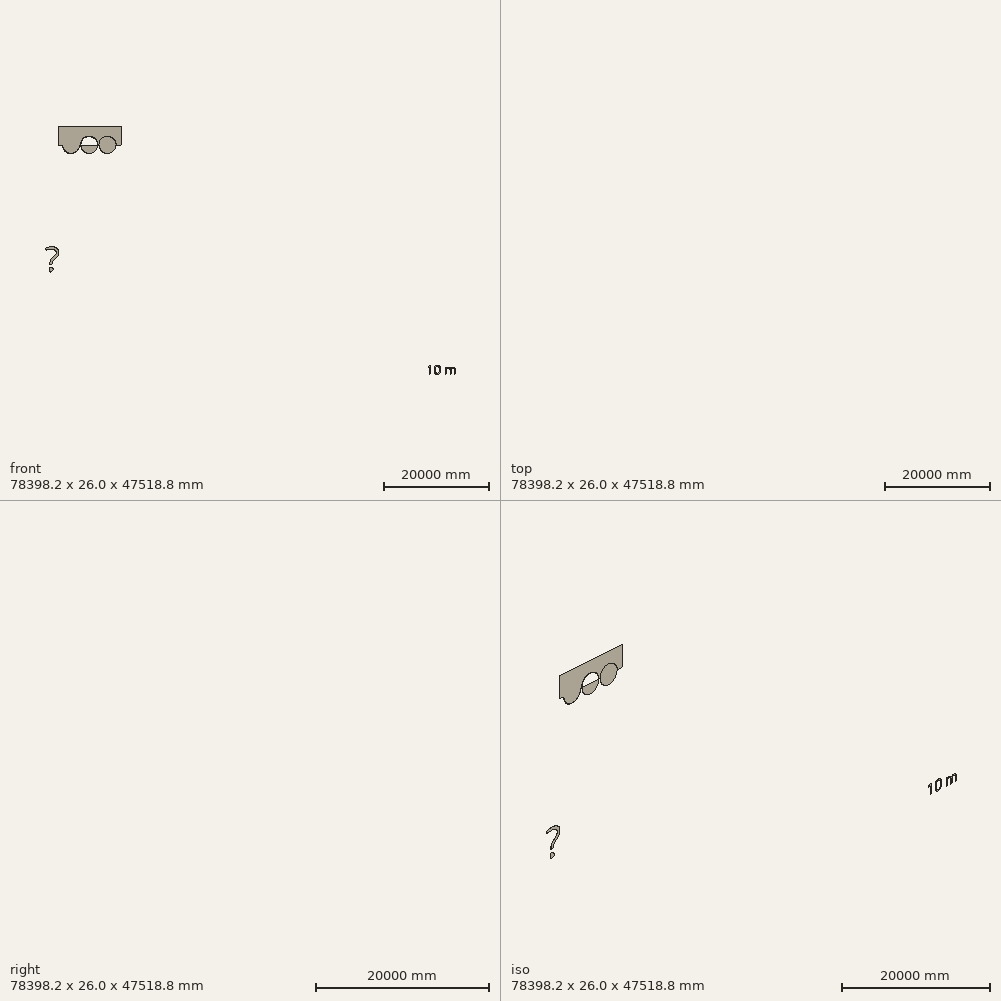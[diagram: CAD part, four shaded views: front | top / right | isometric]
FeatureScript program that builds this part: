
annotation { "Feature Type Name" : "Feature", "Feature Type Description" : "" }
export const myFeature = defineFeature(function(context is Context, id is Id, definition is map)
    precondition{}
    {
        {
            var Q0;
            Q0=qCreatedBy(makeId("Front.planeOp"),FACE);
            var sketch = newSketch(context, id + "F0", { "sketchPlane" : qUnion([Q0])});
            skLineSegment(sketch, "E0", {"start": v(18624.53, 0) * mm, "end": v(-26282.53, 0) * mm});
            skLineSegment(sketch, "E1", {"start": v(-54535.88, 46620.48) * mm, "end": v(-44660.11, 46620.48) * mm});
            skLineSegment(sketch, "E2", {"start": v(-34660.11, 36620.48) * mm, "end": v(-34660.11, 26407.32) * mm});
            skLineSegment(sketch, "E3", {"start": v(-34660.11, 26407.32) * mm, "end": v(-34660.11, 23210.3) * mm});
            skLineSegment(sketch, "E4", {"start": v(-34660.11, 23210.3) * mm, "end": v(-34660.11, 20000) * mm});
            skLineSegment(sketch, "E5", {"start": v(-14660.11, 0) * mm, "end": v(-1994.16, 0) * mm});
            skLineSegment(sketch, "E6", {"start": v(3005.84, 4000) * mm, "end": v(3005.84, 5000) * mm});
            skLineSegment(sketch, "E7", {"start": v(9005.84, 10000) * mm, "end": v(15278.8, 10000) * mm});
            skPoint(sketch, "E8.visualSharp", {"position": v(-34660.11, 46620.48) * mm});
            skArc(sketch, "E8.filletArc", {"start": v(-34660.11, 36620.48) * mm, "mid": v(-37589.04, 43691.54) * mm, "end": v(-44660.11, 46620.48) * mm});
            skPoint(sketch, "E9.visualSharp", {"position": v(-34660.11, 0) * mm});
            skArc(sketch, "E9.filletArc", {"start": v(-34660.11, 20000) * mm, "mid": v(-28802.25, 5857.86) * mm, "end": v(-14660.11, 0) * mm});
            skPoint(sketch, "E10.visualSharp", {"position": v(3005.84, 0) * mm});
            skArc(sketch, "E10.filletArc", {"start": v(-1994.16, 0) * mm, "mid": v(1541.37, 1464.47) * mm, "end": v(3005.84, 5000) * mm});
            skPoint(sketch, "E11.visualSharp", {"position": v(3005.84, 10000) * mm});
            skArc(sketch, "E11.filletArc", {"start": v(9005.84, 10000) * mm, "mid": v(4763.2, 8242.64) * mm, "end": v(3005.84, 4000) * mm});
            skCircle(sketch, "E12", {"center": v(-49592.93, 48230.24) * mm, "radius": 1609.76 * mm});
            skCircle(sketch, "E13", {"center": v(-46111.93, 48230.24) * mm, "radius": 1609.76 * mm});
            skLineSegment(sketch, "E14.bottom", {"start": v(-43471.17, 48230.24) * mm, "end": v(-55474.63, 48230.24) * mm});
            skLineSegment(sketch, "E14.top", {"start": v(-43471.17, 51831.28) * mm, "end": v(-55474.63, 51831.28) * mm});
            skLineSegment(sketch, "E14.left", {"start": v(-43471.17, 48230.24) * mm, "end": v(-43471.17, 51831.28) * mm});
            skLineSegment(sketch, "E14.right", {"start": v(-55474.63, 48230.24) * mm, "end": v(-55474.63, 51831.28) * mm});
            skCircle(sketch, "E15", {"center": v(-53073.94, 48230.24) * mm, "radius": 1609.76 * mm});
            skSolve(sketch);
        }
        {
            var Q0;
            Q0=sQuery(id+"F0.wireOp",EDGE,"E1");
            var Q1;
            Q1=sQuery(id+"F0.wireOp",EDGE,"E2");
            var Q2;
            Q2=sQuery(id+"F0.wireOp",EDGE,"E3");
            var Q3;
            Q3=sQuery(id+"F0.wireOp",EDGE,"E4");
            var Q4;
            Q4=sQuery(id+"F0.wireOp",EDGE,"E6");
            var Q5;
            Q5=sQuery(id+"F0.wireOp",EDGE,"E7");
            var Q6;
            Q6=sQuery(id+"F0.wireOp",EDGE,"E8.filletArc");
            var Q7;
            Q7=sQuery(id+"F0.wireOp",EDGE,"E10.filletArc");
            var Q8;
            Q8=sQuery(id+"F0.wireOp",EDGE,"E11.filletArc");
            var Q9;
            Q9=sQuery(id+"F0.wireOp",EDGE,"E9.filletArc");
            var Q10;
            Q10=sQuery(id+"F0.wireOp",EDGE,"E5");
            extrude(context, id + "F1", {"bodyType" : ToolBodyType.SURFACE, "surfaceEntities" : qUnion([Q0, Q1, Q2, Q3, Q4, Q5, Q6, Q7, Q8, Q9, Q10]), "endBound" : BoundingType.SYMMETRIC, "depth" : 1000 * mm});
        }
        {
            var Q0;
            Q0=makeQuery(id+"F0.imprint","IMPRINT",FACE,{"disambiguationData":[TD([[makeQuery(id+"F0.imprint","IMPRINT",EDGE,{"derivedFrom":sQuery(id+"F0.wireOp",EDGE,"E14.top")}),1.0]])]});
            var Q1;
            {var subQ0=sQuery(id+"F0.wireOp",EDGE,"E14.bottom");var subQ1=sQuery(id+"F0.wireOp",EDGE,"E13");var subQ2=makeQuery(id+"F0.imprint","INTERSECT",VERTEX,{"disambiguationData":[OD(0.0)],"derivedFrom":[subQ1,subQ0]});Q1=makeQuery(id+"F0.imprint","IMPRINT",FACE,{"disambiguationData":[TD([[makeQuery(id+"F0.imprint","IMPRINT",EDGE,{"disambiguationData":[TD([[subQ2,-1.0]])],"derivedFrom":subQ1}),1.0]])]});}
            var Q2;
            {var subQ0=sQuery(id+"F0.wireOp",EDGE,"E13");var subQ1=makeQuery(id+"F0.imprint","INTERSECT",VERTEX,{"derivedFrom":[sQuery(id+"F0.wireOp",EDGE,"E1"),subQ0]});Q2=makeQuery(id+"F0.imprint","IMPRINT",FACE,{"disambiguationData":[TD([[makeQuery(id+"F0.imprint","IMPRINT",EDGE,{"disambiguationData":[TD([[subQ1,1.0]])],"derivedFrom":subQ0}),1.0]])]});}
            var Q3;
            {var subQ0=sQuery(id+"F0.wireOp",EDGE,"E12");var subQ1=makeQuery(id+"F0.imprint","INTERSECT",VERTEX,{"derivedFrom":[sQuery(id+"F0.wireOp",EDGE,"E1"),subQ0]});Q3=makeQuery(id+"F0.imprint","IMPRINT",FACE,{"disambiguationData":[TD([[makeQuery(id+"F0.imprint","IMPRINT",EDGE,{"disambiguationData":[TD([[subQ1,1.0]])],"derivedFrom":subQ0}),1.0]])]});}
            var Q4;
            {var subQ0=sQuery(id+"F0.wireOp",EDGE,"E14.bottom");var subQ1=sQuery(id+"F0.wireOp",EDGE,"E12");var subQ2=makeQuery(id+"F0.imprint","INTERSECT",VERTEX,{"disambiguationData":[OD(0.0)],"derivedFrom":[subQ1,subQ0]});Q4=makeQuery(id+"F0.imprint","IMPRINT",FACE,{"disambiguationData":[TD([[makeQuery(id+"F0.imprint","IMPRINT",EDGE,{"disambiguationData":[TD([[subQ2,1.0]])],"derivedFrom":subQ1}),1.0]])]});}
            var Q5;
            {var subQ0=sQuery(id+"F0.wireOp",EDGE,"E15");var subQ1=sQuery(id+"F0.wireOp",EDGE,"E14.bottom");var subQ2=makeQuery(id+"F0.imprint","INTERSECT",VERTEX,{"disambiguationData":[OD(0.0)],"derivedFrom":[subQ1,subQ0]});Q5=makeQuery(id+"F0.imprint","IMPRINT",FACE,{"disambiguationData":[TD([[makeQuery(id+"F0.imprint","IMPRINT",EDGE,{"disambiguationData":[TD([[subQ2,1.0]])],"derivedFrom":subQ1}),1.0]])]});}
            var Q6;
            {var subQ0=sQuery(id+"F0.wireOp",EDGE,"E15");var subQ1=sQuery(id+"F0.wireOp",EDGE,"E14.bottom");var subQ2=makeQuery(id+"F0.imprint","INTERSECT",VERTEX,{"disambiguationData":[OD(0.0)],"derivedFrom":[subQ1,subQ0]});Q6=makeQuery(id+"F0.imprint","IMPRINT",FACE,{"disambiguationData":[TD([[makeQuery(id+"F0.imprint","IMPRINT",EDGE,{"disambiguationData":[TD([[subQ2,1.0]])],"derivedFrom":subQ1}),-1.0]])]});}
            extrude(context, id + "F2", {"entities" : qUnion([Q0, Q1, Q2, Q3, Q4, Q5, Q6]), "depth" : 25 * mm});
        }
        {
            var Q0;
            Q0=makeQuery(id+"F2.opExtrude","CAP_FACE",FACE,{"disambiguationData":[OSD([sQuery(id+"F0.wireOp",EDGE,"E12"),sQuery(id+"F0.wireOp",EDGE,"E13"),sQuery(id+"F0.wireOp",EDGE,"E14.bottom"),sQuery(id+"F0.wireOp",EDGE,"E14.top"),sQuery(id+"F0.wireOp",EDGE,"E14.left"),sQuery(id+"F0.wireOp",EDGE,"E14.right"),sQuery(id+"F0.wireOp",EDGE,"E15")])],"isStart":false});
            var sketch = newSketch(context, id + "F3", { "sketchPlane" : qUnion([Q0])});
            skCircle(sketch, "E16", {"center": v(-53073.94, 48230.24) * mm, "radius": 1644.99 * mm});
            skCircle(sketch, "E17", {"center": v(-49641.33, 48271.86) * mm, "radius": 1644.99 * mm});
            skCircle(sketch, "E18", {"center": v(-46111.93, 48230.24) * mm, "radius": 1644.99 * mm});
            skSolve(sketch);
        }
        {
            var Q0;
            {var subQ0=sQuery(id+"F3.wireOp",EDGE,"E17");var subQ1=sQuery(id+"F0.wireOp",EDGE,"E12");var subQ2=makeQuery(id+"F2.opExtrude","CAP_EDGE",EDGE,{"disambiguationData":[OSD([subQ1])],"isStart":false});var subQ3=makeQuery(id+"F3.imprint","INTERSECT",VERTEX,{"derivedFrom":[subQ2,subQ0]});Q0=makeQuery(id+"F3.imprint","IMPRINT",FACE,{"disambiguationData":[TD([[makeQuery(id+"F3.imprint","IMPRINT",EDGE,{"disambiguationData":[TD([[subQ3,-1.0]])],"derivedFrom":subQ0}),1.0]])]});}
            var Q1;
            {var subQ2=sQuery(id+"F0.wireOp",EDGE,"E13");var subQ7=makeQuery(id+"F2.opExtrude","CAP_EDGE",EDGE,{"disambiguationData":[OSD([subQ2])],"isStart":false});Q1=makeQuery(id+"F3.imprint","IMPRINT",FACE,{"disambiguationData":[TD([[makeQuery(id+"F3.imprint","IMPRINT",EDGE,{"derivedFrom":subQ7}),1.0]])]});}
            var Q2;
            {var subQ2=sQuery(id+"F0.wireOp",EDGE,"E15");var subQ7=makeQuery(id+"F2.opExtrude","CAP_EDGE",EDGE,{"disambiguationData":[OSD([subQ2])],"isStart":false});Q2=makeQuery(id+"F3.imprint","IMPRINT",FACE,{"disambiguationData":[TD([[makeQuery(id+"F3.imprint","IMPRINT",EDGE,{"derivedFrom":subQ7}),-1.0]])]});}
            extrude(context, id + "F4", {"entities" : qUnion([Q0, Q1, Q2]), "operationType" : NewBodyOperationType.ADD, "depth" : mm});
        }
        {
            var Q0;
            Q0=qCreatedBy(makeId("Front.planeOp"),FACE);
            var sketch = newSketch(context, id + "F5", { "sketchPlane" : qUnion([Q0])});
            skLineSegment(sketch, "E19", {"start": v(-47992.93, 46620.48) * mm, "end": v(-47992.93, 0) * mm});
            skLineSegment(sketch, "E20", {"start": v(-51332.29, 0) * mm, "end": v(-43671.1, 0) * mm});
            skLineSegment(sketch, "E21", {"start": v(-46166, 46620.48) * mm, "end": v(-49724.88, 46620.48) * mm});
            skText(sketch, "E22", { "text": "?", "fontName": "OpenSans-Regular.ttf"});
            const initialGuessF5  = {"E22": [-54.56467, 23.47132, 1, 0, 4.74883]};
            skSetInitialGuess(sketch, initialGuessF5);
            skSolve(sketch);
        }
        {
            var Q0;
            Q0=sQuery(id+"F5.wireOp",EDGE,"E20");
            var Q1;
            Q1=sQuery(id+"F5.wireOp",EDGE,"E21");
            extrude(context, id + "F6", {"bodyType" : ToolBodyType.SURFACE, "surfaceEntities" : qUnion([Q0, Q1]), "depth" : 100 * mm});
        }
        {
            var Q0;
            Q0=qCreatedBy(makeId("Front.planeOp"),FACE);
            var sketch = newSketch(context, id + "F7", { "sketchPlane" : qUnion([Q0])});
            skLineSegment(sketch, "E23", {"start": v(-47793.22, 0) * mm, "end": v(-47793.22, 46392.11) * mm});
            skSolve(sketch);
        }
        {
            var Q0;
            Q0=sQuery(id+"F7.wireOp",EDGE,"E23");
            extrude(context, id + "F8", {"bodyType" : ToolBodyType.SURFACE, "surfaceEntities" : qUnion([Q0]), "depth" : 25 * mm});
        }
        {
            var Q0;
            Q0=qCreatedBy(makeId("Front.planeOp"),FACE);
            var sketch = newSketch(context, id + "F9", { "sketchPlane" : qUnion([Q0])});
            skText(sketch, "E24", { "text": "?", "fontName": "OpenSans-Regular.ttf"});
            const initialGuessF9  = {"E24": [-58.06607, 24.0417, 1, 0, 4.71996]};
            skSetInitialGuess(sketch, initialGuessF9);
            skSolve(sketch);
        }
        {
            var Q0;
            Q0 = qSketchRegion(id + "F9", true);
            extrude(context, id + "F10", {"entities" : qUnion([Q0]), "depth" : 25 * mm});
        }
        {
            var Q0;
            Q0=qCreatedBy(makeId("Front.planeOp"),FACE);
            var sketch = newSketch(context, id + "F11", { "sketchPlane" : qUnion([Q0])});
            skLineSegment(sketch, "E25", {"start": v(11622.77, 0) * mm, "end": v(11622.77, 9743) * mm});
            skLineSegment(sketch, "E26", {"start": v(16481.56, 0) * mm, "end": v(6763.99, 0) * mm});
            skLineSegment(sketch, "E27", {"start": v(9401.61, 9743) * mm, "end": v(13843.93, 9743) * mm});
            skSolve(sketch);
        }
        {
            var Q0;
            Q0 = qSketchRegion(id + "F11", true);
            var Q1;
            Q1=sQuery(id+"F11.wireOp",EDGE,"E27");
            extrude(context, id + "F12", {"entities" : qUnion([Q0]), "bodyType" : ToolBodyType.SURFACE, "surfaceEntities" : qUnion([Q1]), "depth" : 25 * mm});
        }
        {
            var Q0;
            Q0=qCreatedBy(makeId("Front.planeOp"),FACE);
            var sketch = newSketch(context, id + "F13", { "sketchPlane" : qUnion([Q0])});
            skLineSegment(sketch, "E28", {"start": v(11462.3, 9779.33) * mm, "end": v(11462.3, 873.02) * mm});
            skSolve(sketch);
        }
        {
            var Q0;
            Q0 = qSketchRegion(id + "F13", true);
            var Q1;
            Q1=sQuery(id+"F13.wireOp",EDGE,"E28");
            extrude(context, id + "F14", {"entities" : qUnion([Q0]), "bodyType" : ToolBodyType.SURFACE, "surfaceEntities" : qUnion([Q1]), "depth" : 25 * mm});
        }
        {
            var Q0;
            Q0=qCreatedBy(makeId("Front.planeOp"),FACE);
            var sketch = newSketch(context, id + "F15", { "sketchPlane" : qUnion([Q0])});
            skLineSegment(sketch, "E29", {"start": v(7065.5, 882.81) * mm, "end": v(16144.39, 882.81) * mm});
            skSolve(sketch);
        }
        {
            var Q0;
            Q0 = qSketchRegion(id + "F15", true);
            var Q1;
            Q1=sQuery(id+"F15.wireOp",EDGE,"E29");
            extrude(context, id + "F16", {"entities" : qUnion([Q0]), "bodyType" : ToolBodyType.SURFACE, "surfaceEntities" : qUnion([Q1]), "depth" : 25 * mm});
        }
        {
            var Q0;
            Q0=qCreatedBy(makeId("Front.planeOp"),FACE);
            var sketch = newSketch(context, id + "F17", { "sketchPlane" : qUnion([Q0])});
            skText(sketch, "E30", { "text": "10 m\n", "fontName": "OpenSans-Regular.ttf"});
            const initialGuessF17  = {"E30": [14.8615, 4.33674, 1, 0, 1.7763]};
            skSetInitialGuess(sketch, initialGuessF17);
            skSolve(sketch);
        }
        {
            var Q0;
            Q0 = qSketchRegion(id + "F17", true);
            extrude(context, id + "F18", {"entities" : qUnion([Q0]), "depth" : 25 * mm});
        }
    });
